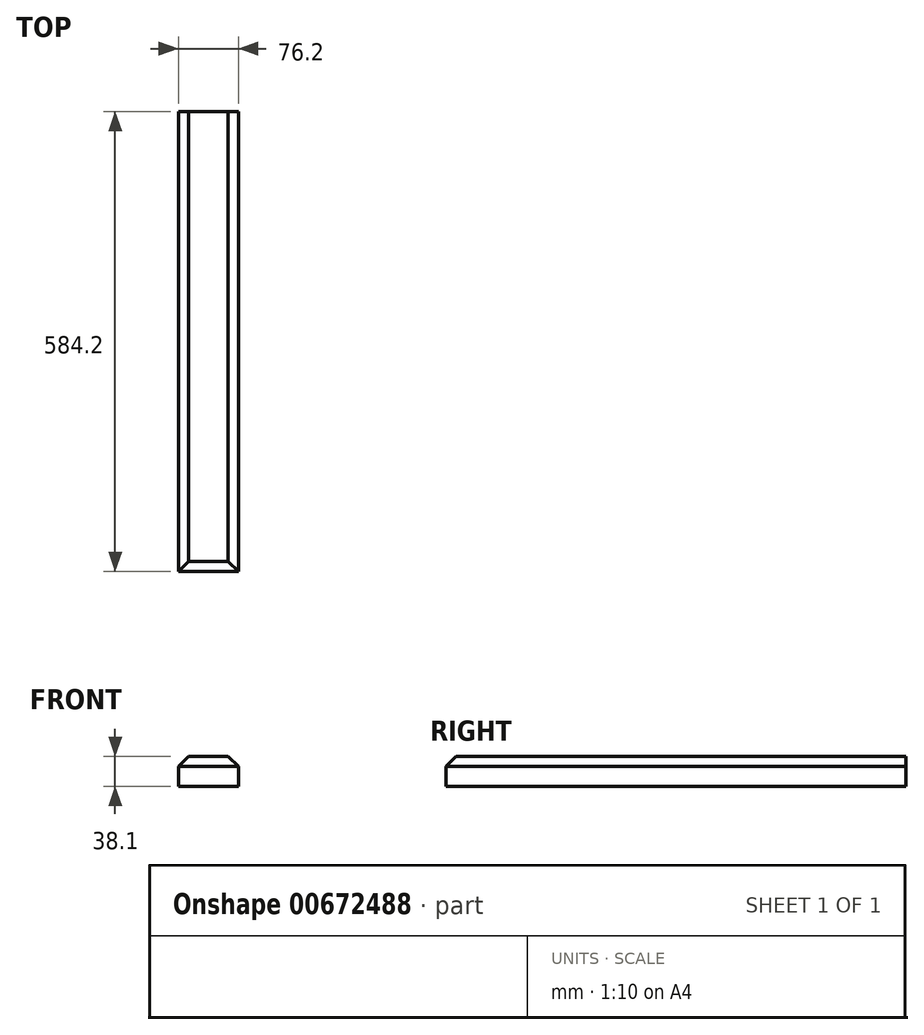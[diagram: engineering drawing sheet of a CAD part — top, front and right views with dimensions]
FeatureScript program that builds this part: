
annotation { "Feature Type Name" : "Feature", "Feature Type Description" : "" }
export const myFeature = defineFeature(function(context is Context, id is Id, definition is map)
    precondition{}
    {
        {
            var Q0;
            Q0=qCreatedBy(makeId("Top.planeOp"),FACE);
            var sketch = newSketch(context, id + "F0", { "sketchPlane" : qUnion([Q0])});
            skLineSegment(sketch, "E0.bottom", {"start": v(-38.1, 292.1) * mm, "end": v(38.1, 292.1) * mm});
            skLineSegment(sketch, "E0.top", {"start": v(-38.1, -292.1) * mm, "end": v(38.1, -292.1) * mm});
            skLineSegment(sketch, "E0.left", {"start": v(-38.1, 292.1) * mm, "end": v(-38.1, -292.1) * mm});
            skLineSegment(sketch, "E0.right", {"start": v(38.1, 292.1) * mm, "end": v(38.1, -292.1) * mm});
            skPoint(sketch, "E1", {"position": v(-38.1, 0) * mm});
            skPoint(sketch, "E2", {"position": v(0, -292.1) * mm});
            skSolve(sketch);
        }
        {
            var Q0;
            Q0=makeQuery(id+"F0.imprint","IMPRINT",FACE,{"disambiguationData":[TD([[makeQuery(id+"F0.imprint","IMPRINT",EDGE,{"derivedFrom":sQuery(id+"F0.wireOp",EDGE,"E0.bottom")}),-1.0]])]});
            extrude(context, id + "F1", {"entities" : qUnion([Q0]), "depth" : 38.1 * mm, "offsetDistance" : 25.4 * mm});
        }
        {
            var Q0;
            Q0=makeQuery(id+"F1.opExtrude","CAP_EDGE",EDGE,{"disambiguationData":[OSD([sQuery(id+"F0.wireOp",EDGE,"E0.top")])],"isStart":false});
            var Q1;
            Q1=makeQuery(id+"F1.opExtrude","CAP_EDGE",EDGE,{"disambiguationData":[OSD([sQuery(id+"F0.wireOp",EDGE,"E0.right")])],"isStart":false});
            var Q2;
            Q2=makeQuery(id+"F1.opExtrude","CAP_EDGE",EDGE,{"disambiguationData":[OSD([sQuery(id+"F0.wireOp",EDGE,"E0.left")])],"isStart":false});
            chamfer(context, id + "F2", {"entities" : qUnion([Q0, Q1, Q2]), "width" : 12.7 * mm, "tangentPropagation" : true});
        }
    });
